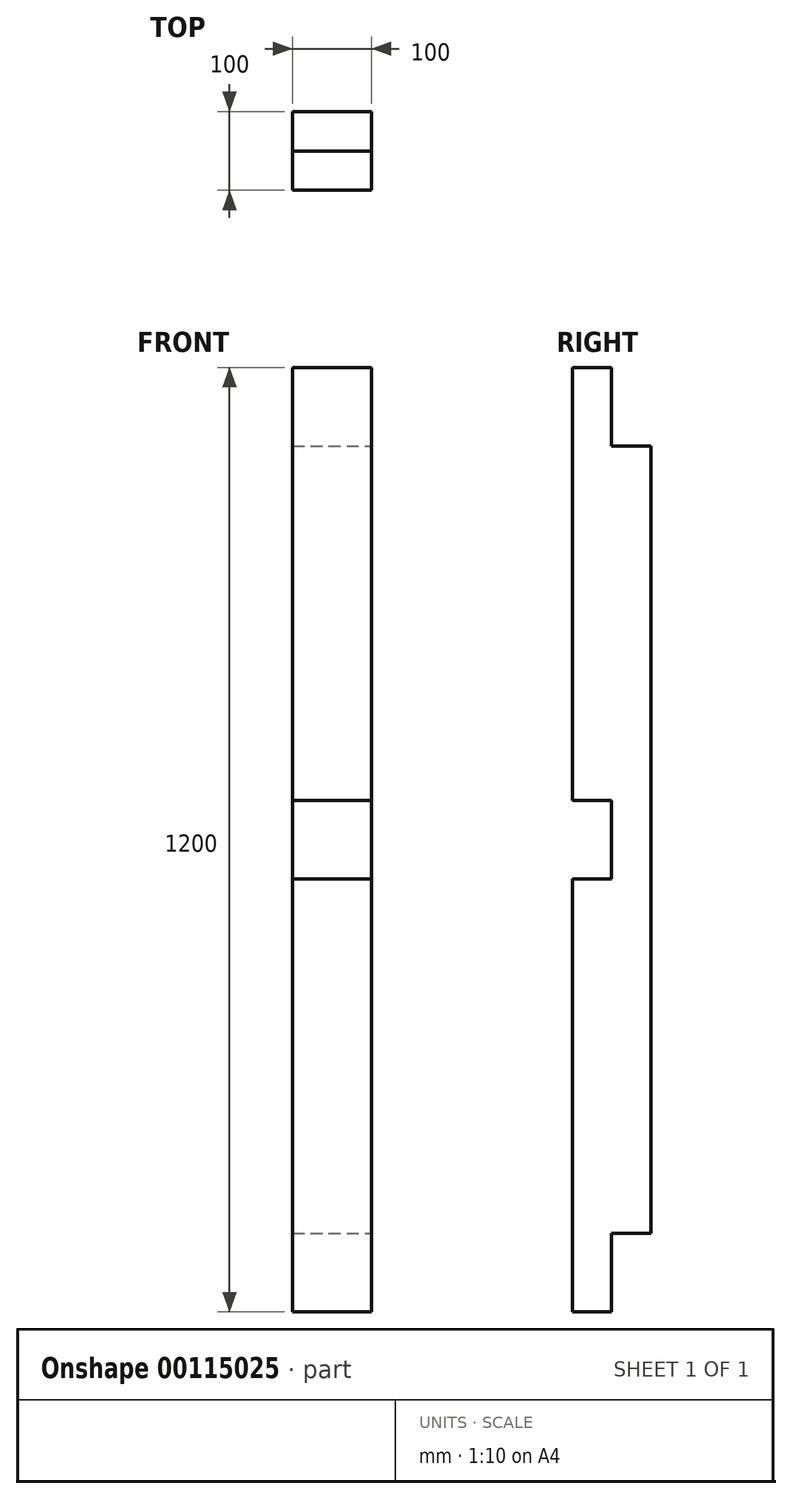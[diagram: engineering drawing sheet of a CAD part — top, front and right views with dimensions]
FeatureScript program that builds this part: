
annotation { "Feature Type Name" : "Feature", "Feature Type Description" : "" }
export const myFeature = defineFeature(function(context is Context, id is Id, definition is map)
    precondition{}
    {
        {
            var Q0;
            Q0=qCreatedBy(makeId("Top.planeOp"),FACE);
            var sketch = newSketch(context, id + "F0", { "sketchPlane" : qUnion([Q0])});
            skLineSegment(sketch, "E0.bottom", {"start": v(50, -50) * mm, "end": v(-50, -50) * mm});
            skLineSegment(sketch, "E0.top", {"start": v(50, 50) * mm, "end": v(-50, 50) * mm});
            skLineSegment(sketch, "E0.left", {"start": v(50, -50) * mm, "end": v(50, 50) * mm});
            skLineSegment(sketch, "E0.right", {"start": v(-50, -50) * mm, "end": v(-50, 50) * mm});
            skPoint(sketch, "E0.middle", {"position": v(0, 0) * mm});
            skSolve(sketch);
        }
        {
            var Q0;
            Q0=qSketchRegion(id+"F0",true);
            extrude(context, id + "F1", {"entities" : qUnion([Q0]), "depth" : 1200 * mm});
        }
        {
            var Q0;
            Q0=makeQuery(id+"F1.opExtrude","SWEPT_FACE",FACE,{"disambiguationData":[OSD([sQuery(id+"F0.wireOp",EDGE,"E0.left")])]});
            var sketch = newSketch(context, id + "F2", { "sketchPlane" : qUnion([Q0])});
            skLineSegment(sketch, "E1.bottom", {"start": v(0, 0) * mm, "end": v(50, 0) * mm});
            skLineSegment(sketch, "E1.top", {"start": v(0, 100) * mm, "end": v(50, 100) * mm});
            skLineSegment(sketch, "E1.left", {"start": v(0, 0) * mm, "end": v(0, 100) * mm});
            skLineSegment(sketch, "E1.right", {"start": v(50, 0) * mm, "end": v(50, 100) * mm});
            skLineSegment(sketch, "E2.bottom", {"start": v(0, 1200) * mm, "end": v(50, 1200) * mm});
            skLineSegment(sketch, "E2.top", {"start": v(0, 1100) * mm, "end": v(50, 1100) * mm});
            skLineSegment(sketch, "E2.left", {"start": v(50, 1200) * mm, "end": v(50, 1100) * mm});
            skLineSegment(sketch, "E2.right", {"start": v(0, 1200) * mm, "end": v(0, 1100) * mm});
            skLineSegment(sketch, "E3.bottom", {"start": v(-50, 550) * mm, "end": v(0, 550) * mm});
            skLineSegment(sketch, "E3.top", {"start": v(-50, 650) * mm, "end": v(0, 650) * mm});
            skLineSegment(sketch, "E3.left", {"start": v(-50, 550) * mm, "end": v(-50, 650) * mm});
            skLineSegment(sketch, "E3.right", {"start": v(0, 550) * mm, "end": v(0, 650) * mm});
            skLineSegment(sketch, "E4", {"start": v(50, 600) * mm, "end": v(0, 600) * mm, "construction": true});
            skSolve(sketch);
        }
        {
            var Q0;
            Q0=qSketchRegion(id+"F2",true);
            extrude(context, id + "F3", {"entities" : qUnion([Q0]), "operationType" : NewBodyOperationType.REMOVE, "endBound" : BoundingType.THROUGH_ALL, "oppositeDirection" : true, "depth" : 25 * mm});
        }
    });
